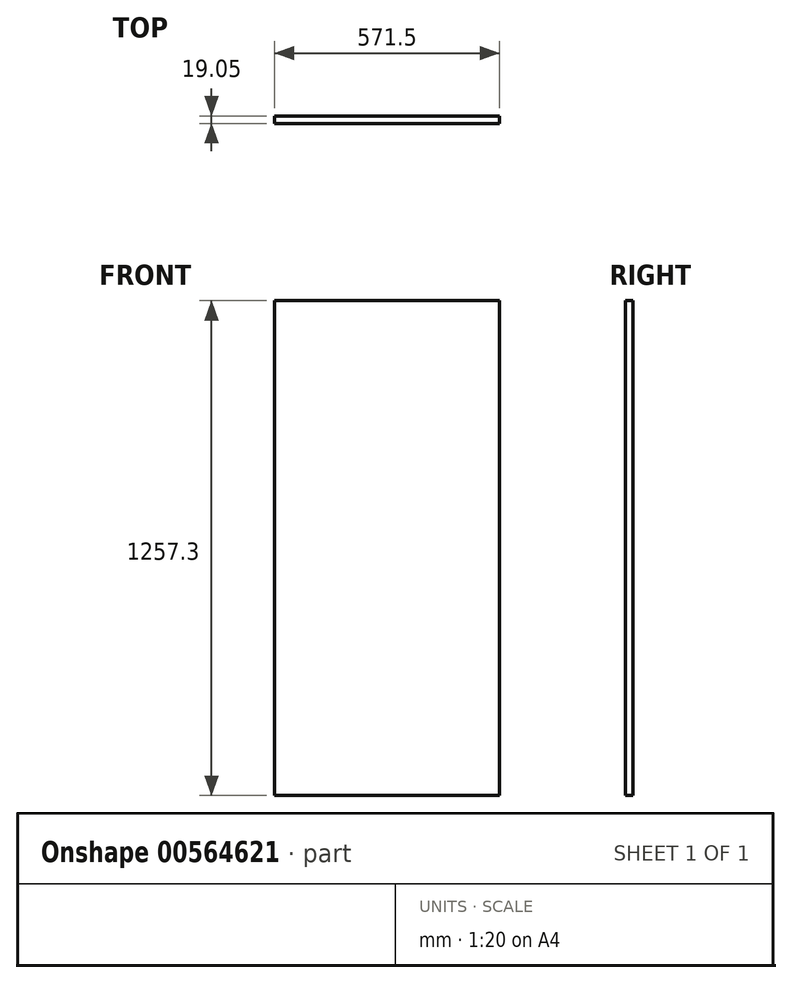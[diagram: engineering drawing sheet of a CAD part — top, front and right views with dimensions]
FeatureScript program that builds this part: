
annotation { "Feature Type Name" : "Feature", "Feature Type Description" : "" }
export const myFeature = defineFeature(function(context is Context, id is Id, definition is map)
    precondition{}
    {
        {
            var Q0;
            Q0=qCreatedBy(makeId("Front.planeOp"),FACE);
            var sketch = newSketch(context, id + "F0", { "sketchPlane" : qUnion([Q0])});
            skLineSegment(sketch, "E0.bottom", {"start": v(285.75, 628.65) * mm, "end": v(-285.75, 628.65) * mm});
            skLineSegment(sketch, "E0.top", {"start": v(285.75, -628.65) * mm, "end": v(-285.75, -628.65) * mm});
            skLineSegment(sketch, "E0.left", {"start": v(285.75, 628.65) * mm, "end": v(285.75, -628.65) * mm});
            skLineSegment(sketch, "E0.right", {"start": v(-285.75, 628.65) * mm, "end": v(-285.75, -628.65) * mm});
            skPoint(sketch, "E0.middle", {"position": v(0, 0) * mm});
            skSolve(sketch);
        }
        {
            var Q0;
            Q0=qSketchRegion(id+"F0",true);
            extrude(context, id + "F1", {"entities" : qUnion([Q0]), "depth" : 19.05 * mm, "offsetDistance" : 25.4 * mm});
        }
    });
